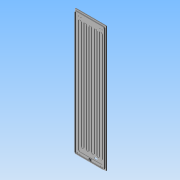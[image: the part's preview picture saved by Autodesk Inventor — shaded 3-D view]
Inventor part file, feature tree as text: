
AUTODESK INVENTOR PART (.ipt)
format: ipt  version: 2013 (Build 170138000, 138)  size: 359,936 bytes
history: native  units: in
note: dims shown in document units (in); Inventor stores cm internally (conversion verified against a paired STEP export)
features: other x14, extrude x4, hole x1, plane x1
ambient origin geometry x8: Origin, YZ Plane, XZ Plane, XY Plane, X Axis, Y Axis, Z Axis, Center Point
bodies: Solid1 (feature_tree)
feature tree (20):
  other  "CHICKA Ply back"
  other  "Blocks"
  extrude  "Stock Extrusion"  Depth=23.8125in
  extrude  "Main rope pocket"  Depth=96.0in
  other  "Side profile reference"
  hole  "Hole1"  [1 undecoded]
  plane  "Work Plane1"
  extrude  "Through Panel Extrusion5"  Depth=86.0in
  extrude  "Outline Channel"  Depth=1.0in
  other  "Stock"
  other  "LEDPocket"
  other  "TwoLineColumn"
  other  "TwoLineColumnEnd"
  other  "15mm Neon profile"
  other  "U Bolt hole and bore"
  other  "U-Bolt holes"
  other  "WeatherProof panel"
  other  "Border"
  other  "15mm Neon profile:1"
  other  "15mm Neon profile:2"
note: 1 required parameter value undecoded (feature->parameter linkage not recoverable at this tier; creation-order binding heuristic only, values carry confidence <= 0.55)
